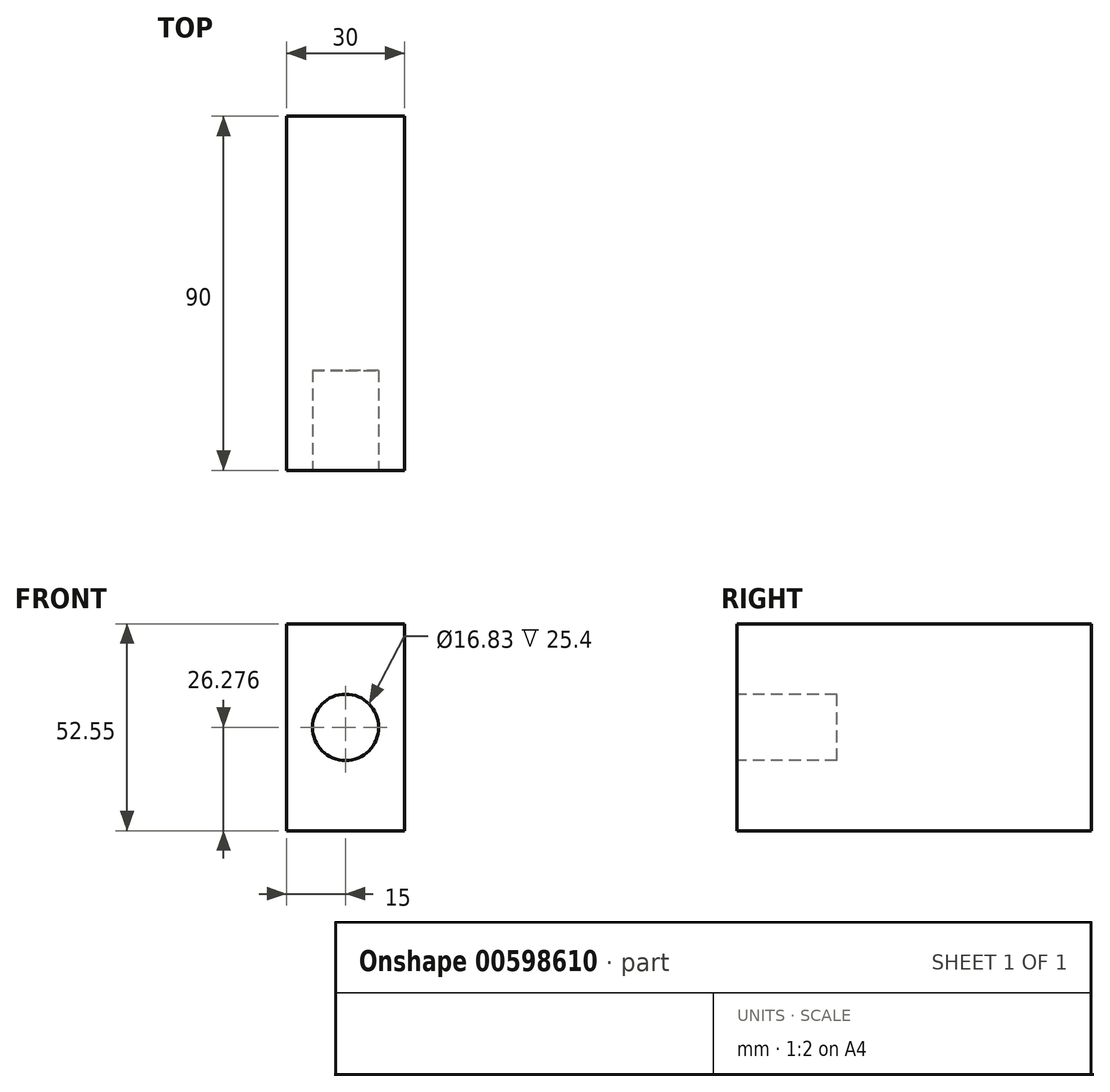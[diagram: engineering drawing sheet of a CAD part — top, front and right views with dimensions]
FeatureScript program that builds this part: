
annotation { "Feature Type Name" : "Feature", "Feature Type Description" : "" }
export const myFeature = defineFeature(function(context is Context, id is Id, definition is map)
    precondition{}
    {
        {
            var Q0;
            Q0=qCreatedBy(makeId("Top.planeOp"),FACE);
            var sketch = newSketch(context, id + "F0", { "sketchPlane" : qUnion([Q0])});
            skLineSegment(sketch, "E0.bottom", {"start": v(15, 45) * mm, "end": v(-15, 45) * mm});
            skLineSegment(sketch, "E0.top", {"start": v(15, -45) * mm, "end": v(-15, -45) * mm});
            skLineSegment(sketch, "E0.left", {"start": v(15, 45) * mm, "end": v(15, -45) * mm});
            skLineSegment(sketch, "E0.right", {"start": v(-15, 45) * mm, "end": v(-15, -45) * mm});
            skPoint(sketch, "E0.middle", {"position": v(0, 0) * mm});
            skSolve(sketch);
        }
        {
            var Q0;
            Q0=makeQuery(id+"F0.imprint","IMPRINT",FACE,{"disambiguationData":[TD([[makeQuery(id+"F0.imprint","IMPRINT",EDGE,{"derivedFrom":sQuery(id+"F0.wireOp",EDGE,"E0.bottom")}),1.0]])]});
            extrude(context, id + "F1", {"entities" : qUnion([Q0]), "depth" : 52.55 * mm, "offsetDistance" : 25.4 * mm});
        }
        {
            var Q0;
            Q0=makeQuery(id+"F1.opExtrude","SWEPT_FACE",FACE,{"disambiguationData":[OSD([sQuery(id+"F0.wireOp",EDGE,"E0.top")])]});
            var sketch = newSketch(context, id + "F2", { "sketchPlane" : qUnion([Q0])});
            skCircle(sketch, "E1", {"center": v(0, 26.28) * mm, "radius": 8.42 * mm});
            skPoint(sketch, "E1.centerSnap0", {"position": v(15, 26.28) * mm});
            skSolve(sketch);
        }
        {
            var Q0;
            Q0 = qSketchRegion(id + "F2", true);
            var Q1;
            Q1=makeQuery(id+"F1.opExtrude","SWEPT_FACE",FACE,{"disambiguationData":[OSD([sQuery(id+"F0.wireOp",EDGE,"E0.bottom")])]});
            extrude(context, id + "F3", {"entities" : qUnion([Q0, Q1]), "operationType" : NewBodyOperationType.REMOVE, "oppositeDirection" : true, "depth" : 25.4 * mm, "offsetDistance" : 25.4 * mm});
        }
    });
